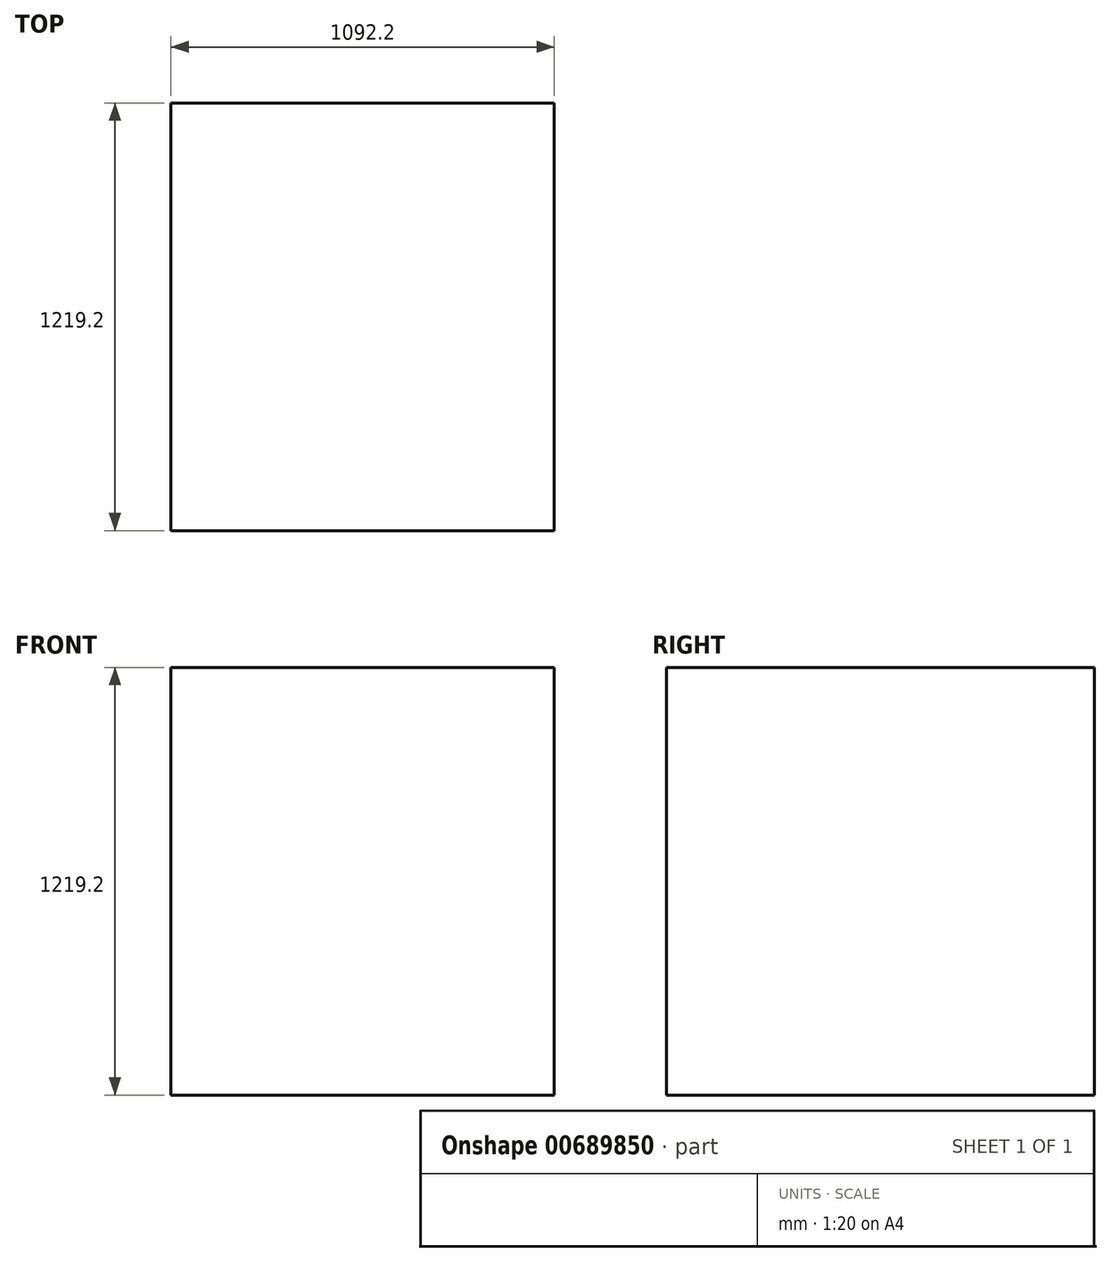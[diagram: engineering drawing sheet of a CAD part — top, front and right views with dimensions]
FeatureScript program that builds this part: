
annotation { "Feature Type Name" : "Feature", "Feature Type Description" : "" }
export const myFeature = defineFeature(function(context is Context, id is Id, definition is map)
    precondition{}
    {
        {
            var Q0;
            Q0=qCreatedBy(makeId("Top.planeOp"),FACE);
            var sketch = newSketch(context, id + "F0", { "sketchPlane" : qUnion([Q0])});
            skLineSegment(sketch, "E0.bottom", {"start": v(-546.1, -609.6) * mm, "end": v(546.1, -609.6) * mm});
            skLineSegment(sketch, "E0.top", {"start": v(-546.1, 609.6) * mm, "end": v(546.1, 609.6) * mm});
            skLineSegment(sketch, "E0.left", {"start": v(-546.1, -609.6) * mm, "end": v(-546.1, 609.6) * mm});
            skLineSegment(sketch, "E0.right", {"start": v(546.1, -609.6) * mm, "end": v(546.1, 609.6) * mm});
            skPoint(sketch, "E0.middle", {"position": v(0, 0) * mm});
            skSolve(sketch);
        }
        {
            var Q0;
            Q0 = qSketchRegion(id + "F0", true);
            extrude(context, id + "F1", {"entities" : qUnion([Q0]), "endBound" : BoundingType.SYMMETRIC, "depth" : 1219.2 * mm, "offsetDistance" : 25.4 * mm});
        }
    });
